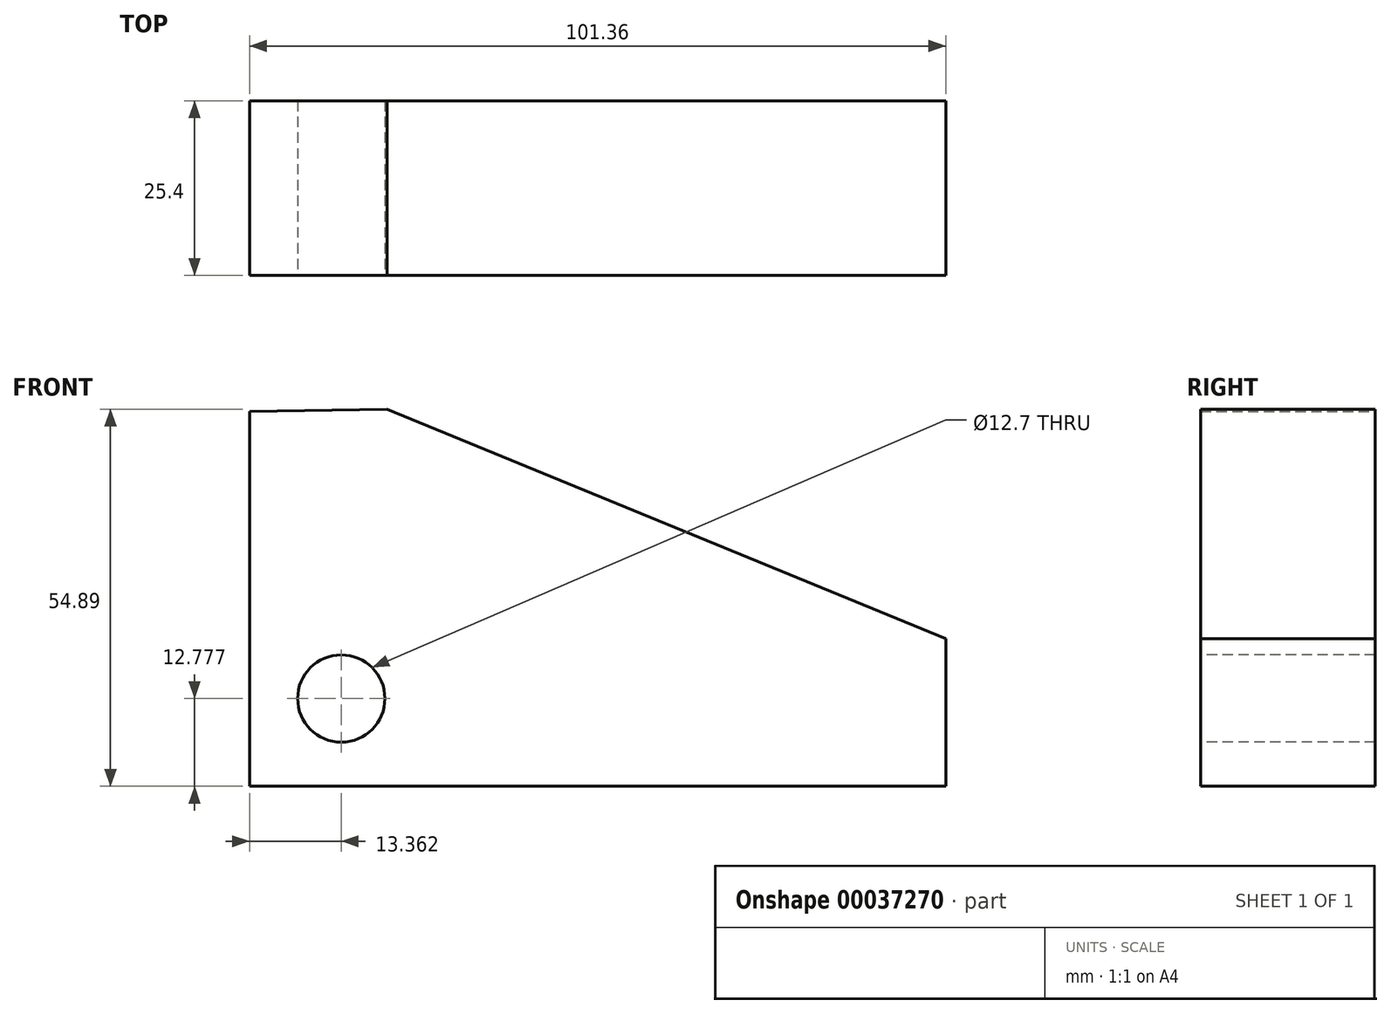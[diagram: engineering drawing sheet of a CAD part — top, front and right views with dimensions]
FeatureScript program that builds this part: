
annotation { "Feature Type Name" : "Feature", "Feature Type Description" : "" }
export const myFeature = defineFeature(function(context is Context, id is Id, definition is map)
    precondition{}
    {
        {
            var Q0;
            Q0=qCreatedBy(makeId("Front.planeOp"),FACE);
            var sketch = newSketch(context, id + "F0", { "sketchPlane" : qUnion([Q0])});
            skLineSegment(sketch, "E0", {"start": v(-46.76, 29.19) * mm, "end": v(-46.76, -25.41) * mm});
            skLineSegment(sketch, "E1", {"start": v(-46.76, -25.41) * mm, "end": v(54.6, -25.41) * mm});
            skLineSegment(sketch, "E2", {"start": v(54.6, -25.41) * mm, "end": v(54.6, -3.92) * mm});
            skLineSegment(sketch, "E3", {"start": v(54.6, -3.92) * mm, "end": v(-26.72, 29.48) * mm});
            skLineSegment(sketch, "E4", {"start": v(-26.72, 29.48) * mm, "end": v(-46.76, 29.19) * mm});
            skSolve(sketch);
        }
        {
            var Q0;
            Q0=makeQuery(id+"F0.imprint","IMPRINT",FACE,{"disambiguationData":[TD([[makeQuery(id+"F0.imprint","IMPRINT",EDGE,{"derivedFrom":sQuery(id+"F0.wireOp",EDGE,"E0")}),1.0]])]});
            extrude(context, id + "F1", {"entities" : qUnion([Q0]), "depth" : 25.4 * mm});
        }
        {
            var Q0;
            Q0=makeQuery(id+"F1.opExtrude","CAP_FACE",FACE,{"disambiguationData":[OSD([sQuery(id+"F0.wireOp",EDGE,"E0"),sQuery(id+"F0.wireOp",EDGE,"E1"),sQuery(id+"F0.wireOp",EDGE,"E2"),sQuery(id+"F0.wireOp",EDGE,"E3"),sQuery(id+"F0.wireOp",EDGE,"E4")])],"isStart":false});
            var sketch = newSketch(context, id + "F2", { "sketchPlane" : qUnion([Q0])});
            skCircle(sketch, "E5", {"center": v(-33.4, -12.63) * mm, "radius": 7.03 * mm});
            skSolve(sketch);
        }
        {
            var Q0;
            Q0=sQuery(id+"F2.wireOp",VERTEX,"E5.center");
            var Q1;
            Q1=makeQuery(id+"F1.opExtrude","SWEPT_BODY",BODY,{"disambiguationData":[OSD([sQuery(id+"F0.wireOp",EDGE,"E0"),sQuery(id+"F0.wireOp",EDGE,"E1"),sQuery(id+"F0.wireOp",EDGE,"E2"),sQuery(id+"F0.wireOp",EDGE,"E3"),sQuery(id+"F0.wireOp",EDGE,"E4")])]});
            hole(context, id + "F3", {"style" : HoleStyle.SIMPLE, "holeDiameter" : 12.7 * mm, "endStyle" : HoleEndStyle.THROUGH, "locations" : qUnion([Q0]), "scope" : qUnion([Q1])});
        }
    });
